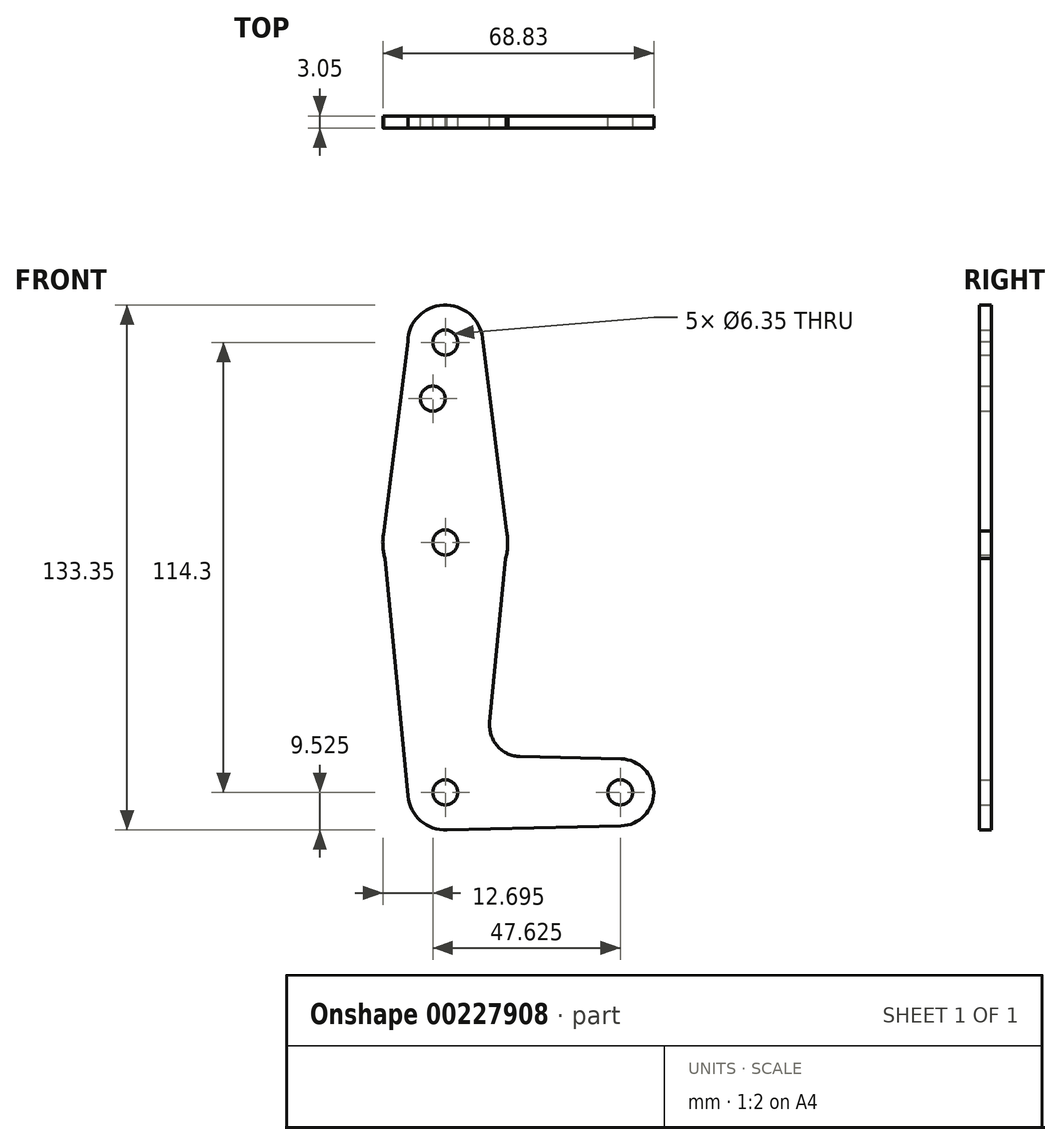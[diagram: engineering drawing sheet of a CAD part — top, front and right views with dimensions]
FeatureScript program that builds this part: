
annotation { "Feature Type Name" : "Feature", "Feature Type Description" : "" }
export const myFeature = defineFeature(function(context is Context, id is Id, definition is map)
    precondition{}
    {
        {
            var Q0;
            Q0=qCreatedBy(makeId("Front.planeOp"),FACE);
            var sketch = newSketch(context, id + "F0", { "sketchPlane" : qUnion([Q0])});
            skLineSegment(sketch, "E0", {"start": v(0, 73.8) * mm, "end": v(0, -40.5) * mm});
            skLineSegment(sketch, "E1", {"start": v(0, -40.5) * mm, "end": v(44.45, -40.5) * mm});
            skCircle(sketch, "E2", {"center": v(0, 73.8) * mm, "radius": 9.53 * mm});
            skCircle(sketch, "E3", {"center": v(0, 23) * mm, "radius": 15.88 * mm});
            skCircle(sketch, "E4", {"center": v(0, -40.5) * mm, "radius": 9.53 * mm});
            skCircle(sketch, "E5", {"center": v(44.45, -40.5) * mm, "radius": 8.5 * mm});
            skLineSegment(sketch, "E6", {"start": v(0, 23) * mm, "end": v(0, -40.5) * mm});
            skLineSegment(sketch, "E7", {"start": v(-9.52, 74.01) * mm, "end": v(-15.75, 25) * mm});
            skLineSegment(sketch, "E8", {"start": v(-15.75, 25) * mm, "end": v(-15.34, 18.93) * mm});
            skLineSegment(sketch, "E9", {"start": v(15.34, 18.93) * mm, "end": v(15.84, 24.05) * mm});
            skLineSegment(sketch, "E10", {"start": v(15.84, 24.05) * mm, "end": v(9.45, 75) * mm});
            skLineSegment(sketch, "E11", {"start": v(15.34, 18.93) * mm, "end": v(11.3, -22.69) * mm});
            skLineSegment(sketch, "E12", {"start": v(-15.34, 18.93) * mm, "end": v(-9.48, -41.42) * mm});
            skLineSegment(sketch, "E13", {"start": v(19.03, -31.4) * mm, "end": v(44.64, -31.99) * mm});
            skLineSegment(sketch, "E14", {"start": v(0, -50.02) * mm, "end": v(44.64, -49) * mm});
            skCircle(sketch, "E15", {"center": v(0, 73.8) * mm, "radius": 3.18 * mm});
            skCircle(sketch, "E16", {"center": v(0, 23) * mm, "radius": 3.18 * mm});
            skCircle(sketch, "E17", {"center": v(0, -40.5) * mm, "radius": 3.18 * mm});
            skCircle(sketch, "E18", {"center": v(44.45, -40.5) * mm, "radius": 3.18 * mm});
            skCircle(sketch, "E19", {"center": v(-3.17, 59.53) * mm, "radius": 3.18 * mm});
            skPoint(sketch, "E20.newPointB", {"position": v(0, -30.97) * mm});
            skArc(sketch, "E20.filletArc", {"start": v(11.3, -22.69) * mm, "mid": v(13.27, -28.73) * mm, "end": v(19.03, -31.4) * mm});
            skSolve(sketch);
        }
        {
            var Q0;
            Q0 = qSketchRegion(id + "F0", true);
            var Q1;
            {var subQ0=sQuery(id+"F0.wireOp",EDGE,"E17");var subQ1=sQuery(id+"F0.wireOp",EDGE,"E1");var subQ2=makeQuery(id+"F0.imprint","INTERSECT",VERTEX,{"derivedFrom":[subQ1,subQ0]});Q1=makeQuery(id+"F0.imprint","IMPRINT",FACE,{"disambiguationData":[TD([[makeQuery(id+"F0.imprint","IMPRINT",EDGE,{"disambiguationData":[TD([[subQ2,-1.0]])],"derivedFrom":subQ1}),1.0]])]});}
            extrude(context, id + "F1", {"entities" : qUnion([Q0, Q1]), "depth" : 3.05 * mm});
        }
    });
